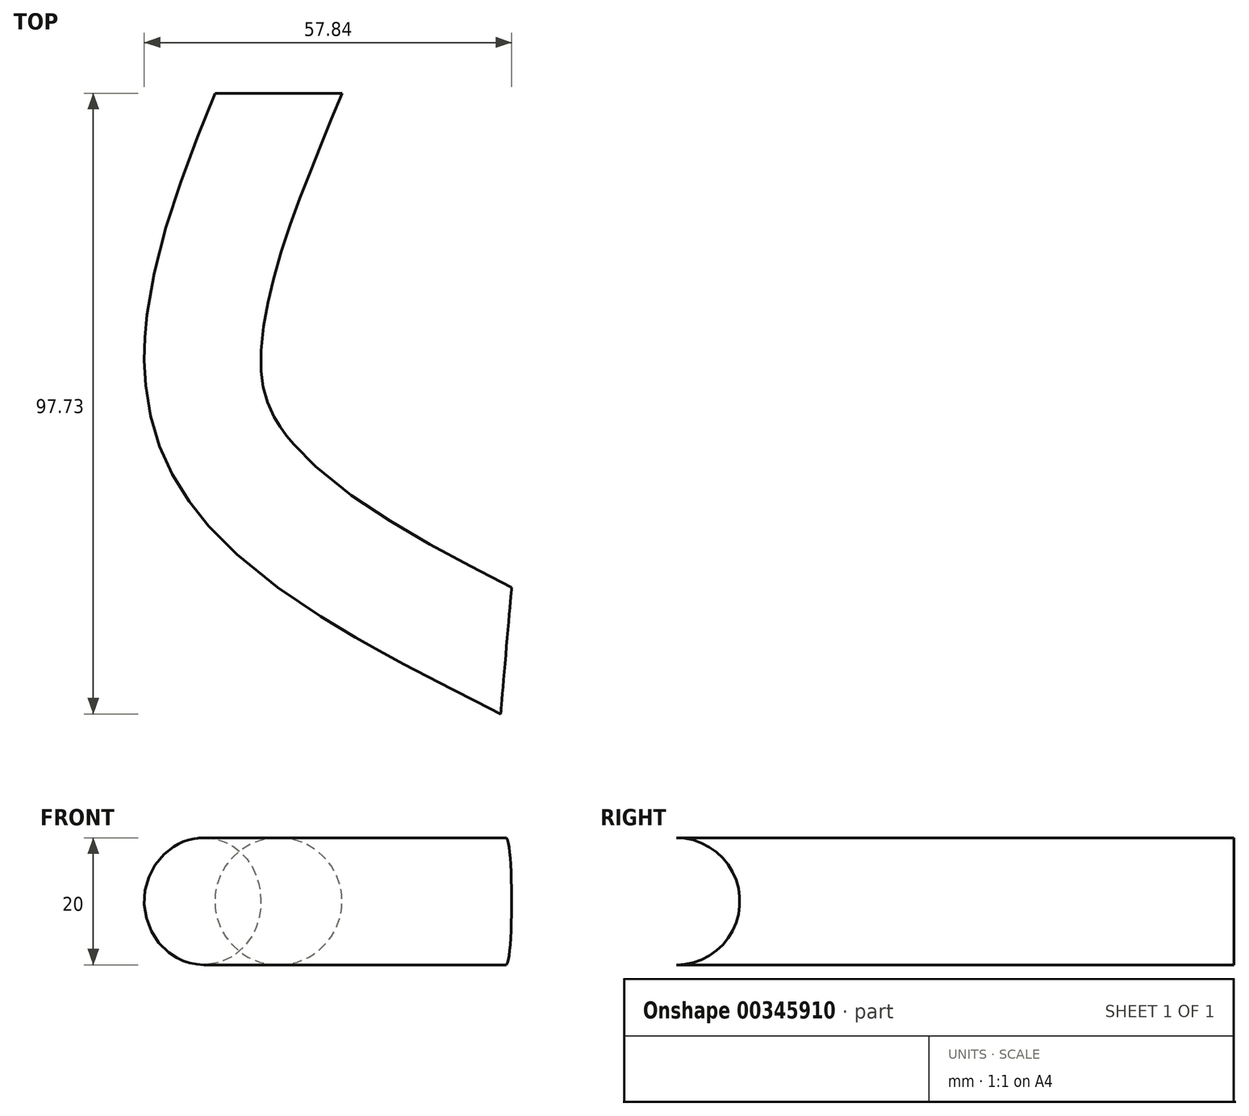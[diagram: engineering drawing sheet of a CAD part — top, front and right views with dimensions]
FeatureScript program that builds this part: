
annotation { "Feature Type Name" : "Feature", "Feature Type Description" : "" }
export const myFeature = defineFeature(function(context is Context, id is Id, definition is map)
    precondition{}
    {
        {
            var Q0;
            Q0=qCreatedBy(makeId("Front.planeOp"),FACE);
            var sketch = newSketch(context, id + "F0", { "sketchPlane" : qUnion([Q0])});
            skCircle(sketch, "E0", {"center": v(0, 0) * mm, "radius": 10 * mm});
            skSolve(sketch);
        }
        {
            var Q0;
            Q0=qCreatedBy(makeId("Top.planeOp"),FACE);
            var sketch = newSketch(context, id + "F1", { "sketchPlane" : qUnion([Q0])});
            skFitSpline(sketch, "E1", {"points": [v(0, 0) * mm, v(-9.88, -52.29) * mm, v(35.85, -87.77) * mm], "startDerivative": vector(-47.06, -115.95) * mm, "endDerivative": vector(117.6, -59.98) * mm});
            skSolve(sketch);
        }
        {
            var Q0;
            Q0=makeQuery(id+"F0.imprint","IMPRINT",FACE,{"disambiguationData":[TD([[makeQuery(id+"F0.imprint","IMPRINT",EDGE,{"derivedFrom":sQuery(id+"F0.wireOp",EDGE,"E0")}),1.0]])]});
            var Q1;
            Q1=sQuery(id+"F1.wireOp",EDGE,"E1");
            sweep(context, id + "F2", {"profiles" : qUnion([Q0]), "path" : qUnion([Q1])});
        }
    });
